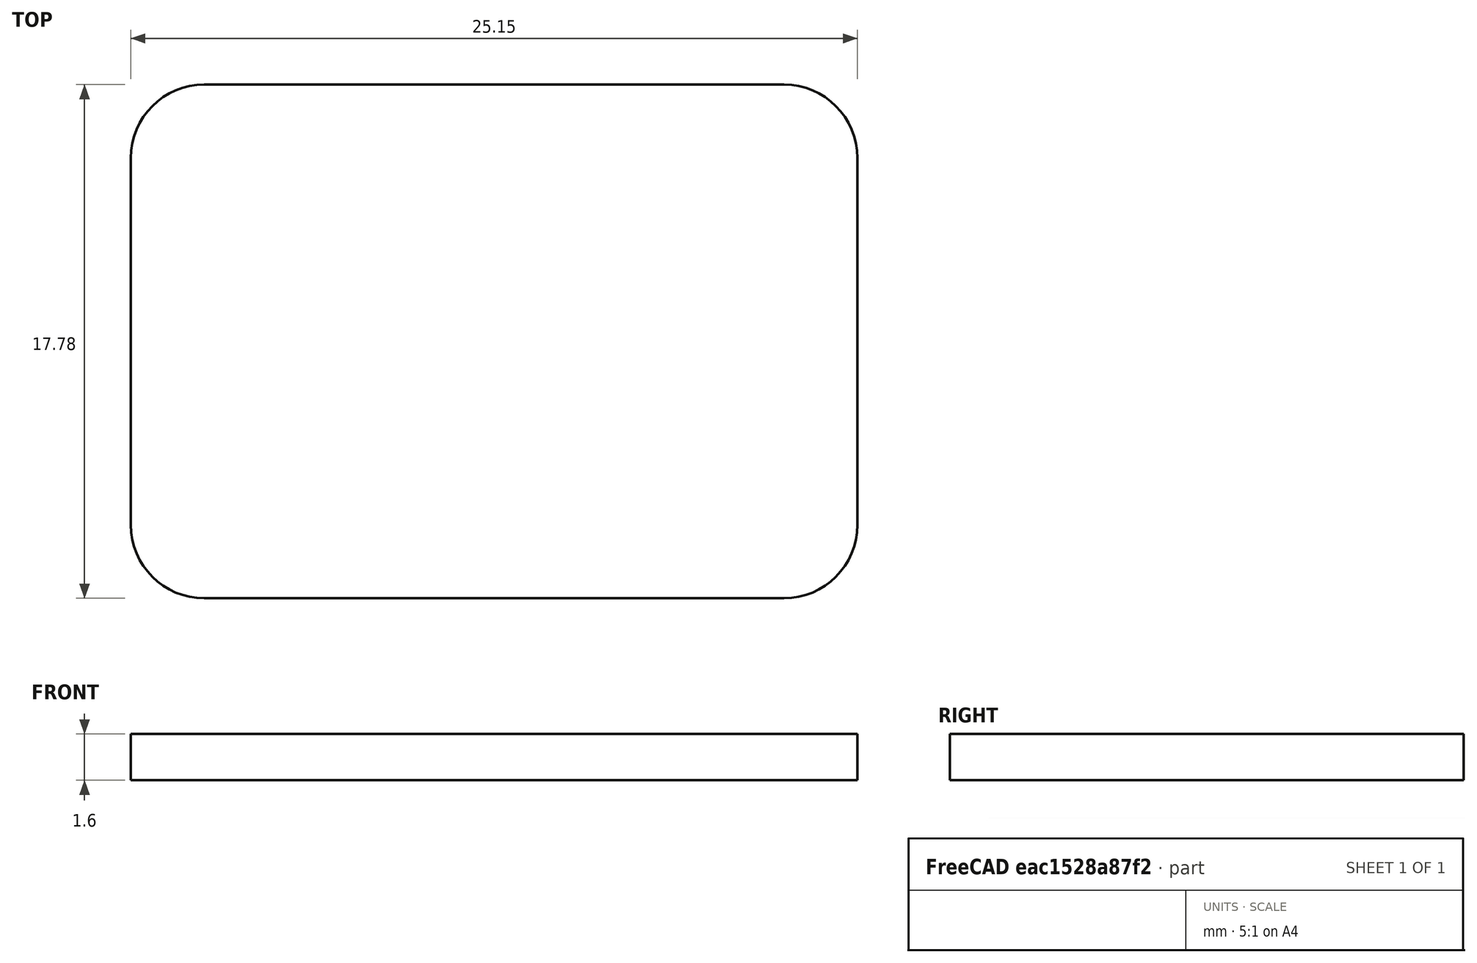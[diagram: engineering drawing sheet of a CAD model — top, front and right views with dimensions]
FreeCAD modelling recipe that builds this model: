
FCSTD DOCUMENT  (FreeCAD 0.16R6078 (Git))
Label: TTStrobe
License: All rights reserved
LicenseURL: http://en.wikipedia.org/wiki/All_rights_reserved
objects: Sketcher::SketchObject×1, PartDesign::Pad×1
note: 3 computed .brp shape members not serialized (recipe doc carries the construction recipe); baked Part::Feature solids carry a one-line shape summary decoded from their .brp

FEATURE [Sketcher::SketchObject] Sketch
  sketch-geometry (8):
    g0: LineSegment StartX=2.54 StartY=17.78 StartZ=0 EndX=22.606 EndY=17.78 EndZ=0
    g1: LineSegment StartX=25.146 StartY=15.24 StartZ=0 EndX=25.146 EndY=2.54 EndZ=0
    g2: LineSegment StartX=22.606 StartY=0 StartZ=0 EndX=2.54 EndY=0 EndZ=0
    g3: LineSegment StartX=0 StartY=2.54 StartZ=0 EndX=0 EndY=15.24 EndZ=0
    g4: ArcOfCircle CenterX=2.54 CenterY=15.24 CenterZ=0 NormalX=0 NormalY=0 NormalZ=1 Radius=2.54 StartAngle=1.5708 EndAngle=3.14159
    g5: ArcOfCircle CenterX=22.606 CenterY=2.54 CenterZ=0 NormalX=0 NormalY=0 NormalZ=1 Radius=2.54 StartAngle=4.71239 EndAngle=6.28319
    g6: ArcOfCircle CenterX=22.606 CenterY=15.24 CenterZ=0 NormalX=0 NormalY=0 NormalZ=1 Radius=2.54 StartAngle=0 EndAngle=1.5708
    g7: ArcOfCircle CenterX=2.54 CenterY=2.54 CenterZ=0 NormalX=0 NormalY=0 NormalZ=1 Radius=2.54 StartAngle=3.14159 EndAngle=4.71239
  constraints (20):
    c: Horizontal(g0)
    c: Horizontal(g2)
    c: Vertical(g1)
    c: Vertical(g3)
    c: Tangent(g0,g4) = 1.5708
    c: Tangent(g3,g4) = 1.5708
    c: Tangent(g1,g5) = 1.5708
    c: Tangent(g2,g5) = 1.5708
    c: Radius(g4) = 2.54
    c: Equal(g5,g4)
    c: Tangent(g0,g6) = 1.5708
    c: Tangent(g1,g6) = 1.5708
    c: Tangent(g3,g7) = 1.5708
    c: Tangent(g2,g7) = 1.5708
    c: Equal(g6,g4)
    c: Equal(g7,g4)
    c: Distance(g0,g2) = 17.78
    c: Distance(g3,g1) = 25.146
    c: DistanceY(g-1,g3) = 2.54
    c: DistanceX(g-1,g2) = 2.54
FEATURE [PartDesign::Pad] Pad
  Length = 1.6
  Length2 = 100
  Sketch = -> Sketch
  Type = 0
